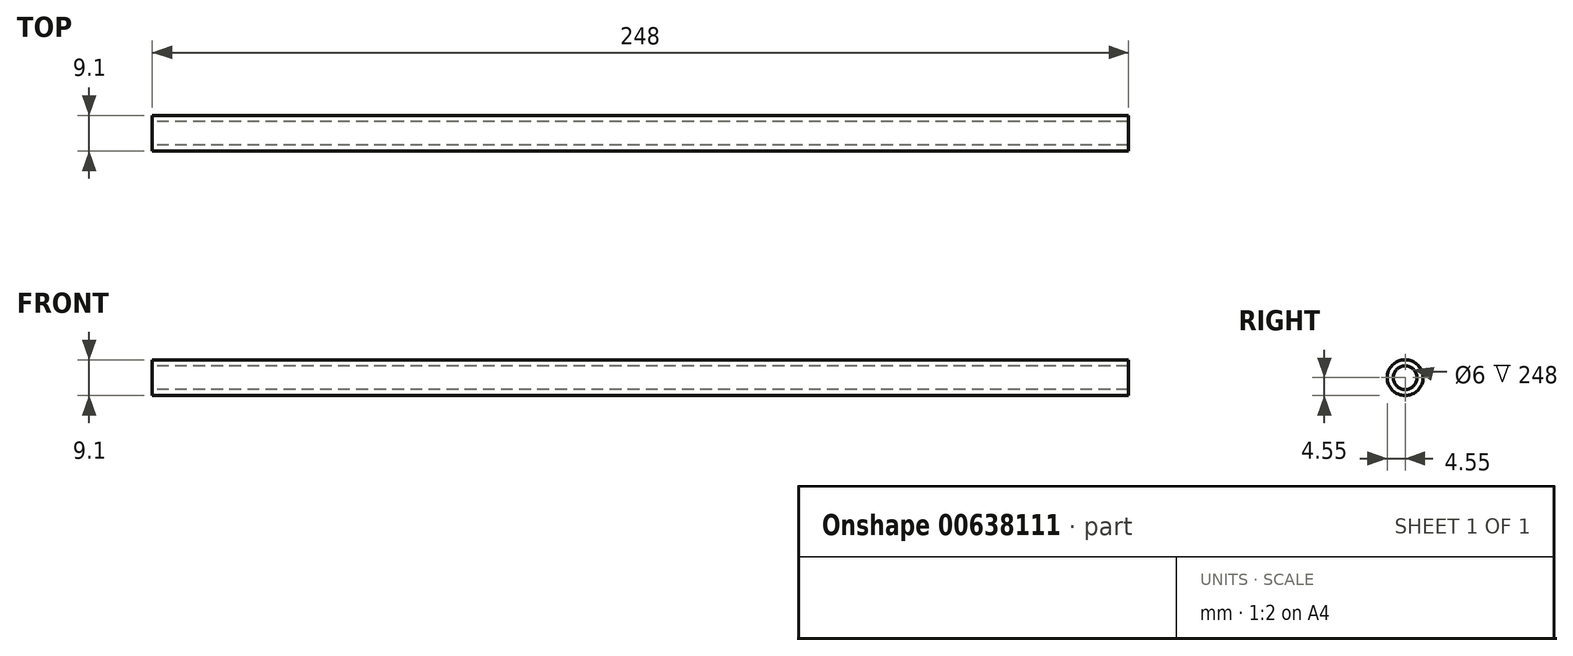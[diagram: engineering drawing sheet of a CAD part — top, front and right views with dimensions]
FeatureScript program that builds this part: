
annotation { "Feature Type Name" : "Feature", "Feature Type Description" : "" }
export const myFeature = defineFeature(function(context is Context, id is Id, definition is map)
    precondition{}
    {
        {
            var Q0;
            Q0=qCreatedBy(makeId("Right.planeOp"),FACE);
            var sketch = newSketch(context, id + "F0", { "sketchPlane" : qUnion([Q0])});
            skCircle(sketch, "E0", {"center": v(0, 0) * mm, "radius": 3 * mm});
            skCircle(sketch, "E1", {"center": v(0, 0) * mm, "radius": 4.55 * mm});
            skSolve(sketch);
        }
        {
            var Q0;
            Q0=makeQuery(id+"F0.imprint","IMPRINT",FACE,{"disambiguationData":[TD([[makeQuery(id+"F0.imprint","IMPRINT",EDGE,{"derivedFrom":sQuery(id+"F0.wireOp",EDGE,"E0")}),-1.0]])]});
            extrude(context, id + "F1", {"entities" : qUnion([Q0]), "depth" : 248 * mm, "offsetDistance" : 25 * mm});
        }
    });
